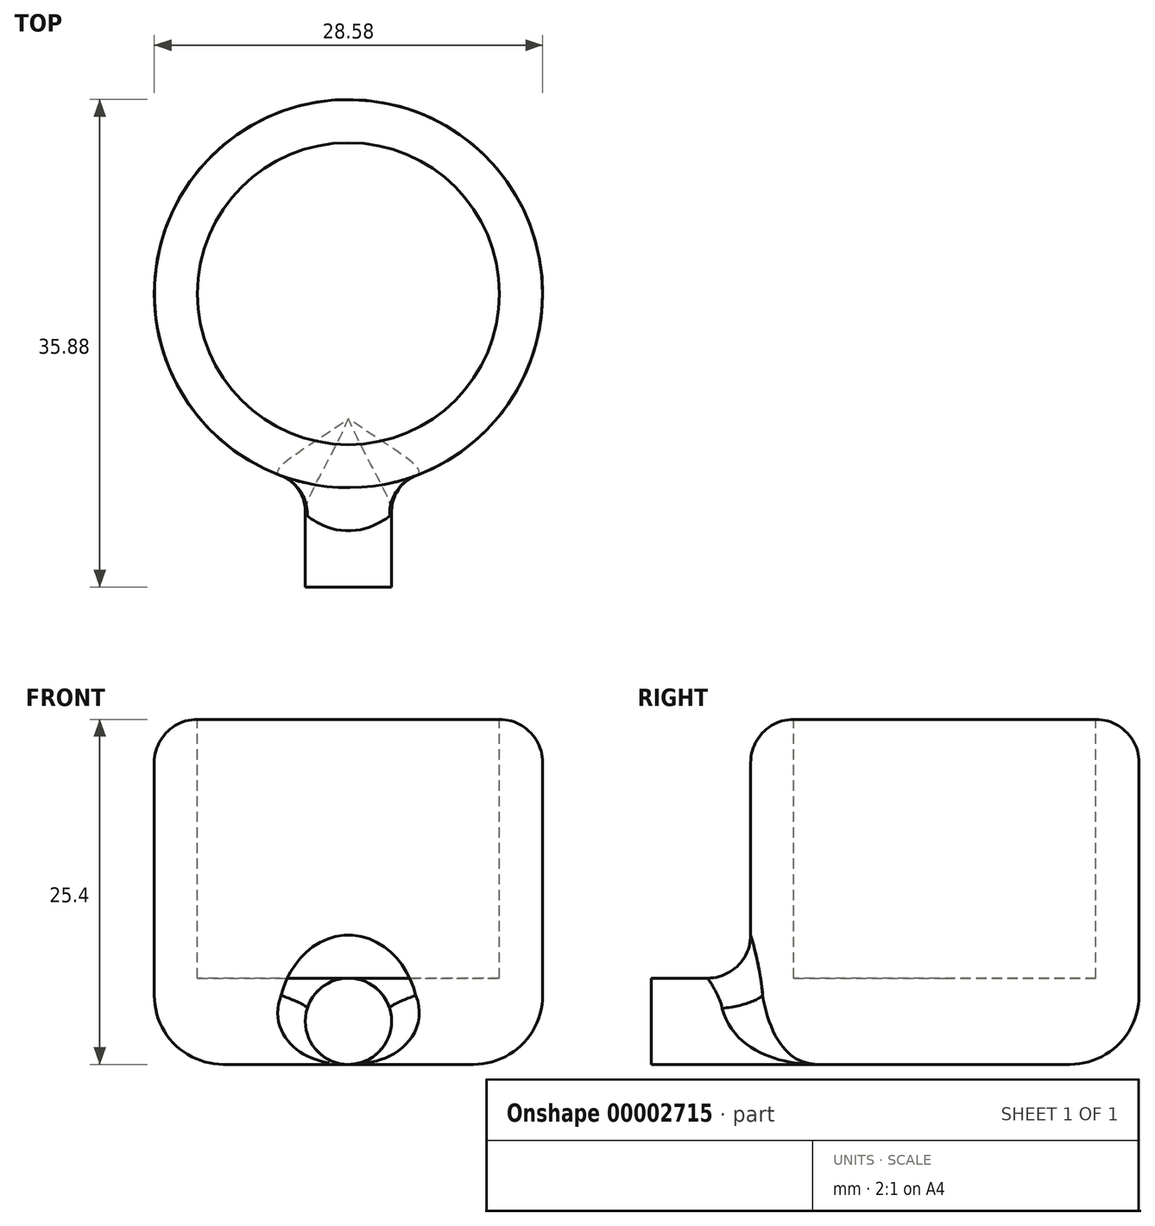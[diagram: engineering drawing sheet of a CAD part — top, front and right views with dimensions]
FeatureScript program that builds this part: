
annotation { "Feature Type Name" : "Feature", "Feature Type Description" : "" }
export const myFeature = defineFeature(function(context is Context, id is Id, definition is map)
    precondition{}
    {
        {
            var Q0;
            Q0=qCreatedBy(makeId("Top.planeOp"),FACE);
            var sketch = newSketch(context, id + "F0", { "sketchPlane" : qUnion([Q0])});
            skCircle(sketch, "E0", {"center": v(0, 0) * mm, "radius": 14.29 * mm});
            skSolve(sketch);
        }
        {
            var Q0;
            Q0=makeQuery(id+"F0.imprint","IMPRINT",FACE,{"disambiguationData":[TD([[makeQuery(id+"F0.imprint","IMPRINT",EDGE,{"derivedFrom":sQuery(id+"F0.wireOp",EDGE,"E0")}),1.0]])]});
            extrude(context, id + "F1", {"entities" : qUnion([Q0]), "depth" : 25.4 * mm});
        }
        {
            var Q0;
            Q0=qCreatedBy(makeId("Front.planeOp"),FACE);
            var sketch = newSketch(context, id + "F2", { "sketchPlane" : qUnion([Q0])});
            skCircle(sketch, "E1", {"center": v(0, 3.18) * mm, "radius": 3.18 * mm});
            skSolve(sketch);
        }
        {
            var Q0;
            Q0=makeQuery(id+"F2.imprint","IMPRINT",FACE,{"disambiguationData":[TD([[makeQuery(id+"F2.imprint","IMPRINT",EDGE,{"derivedFrom":sQuery(id+"F2.wireOp",EDGE,"E1")}),1.0]])]});
            extrude(context, id + "F3", {"entities" : qUnion([Q0]), "operationType" : NewBodyOperationType.ADD, "depth" : 21.59 * mm});
        }
        {
            var Q0;
            Q0=makeQuery(id+"F1.opExtrude","CAP_FACE",FACE,{"disambiguationData":[OSD([sQuery(id+"F0.wireOp",EDGE,"E0")])],"isStart":false});
            var sketch = newSketch(context, id + "F4", { "sketchPlane" : qUnion([Q0])});
            skCircle(sketch, "E2", {"center": v(0, 0) * mm, "radius": 11.11 * mm});
            skSolve(sketch);
        }
        {
            var Q0;
            Q0=makeQuery(id+"F4.imprint","IMPRINT",FACE,{"disambiguationData":[TD([[makeQuery(id+"F4.imprint","IMPRINT",EDGE,{"derivedFrom":sQuery(id+"F4.wireOp",EDGE,"E2")}),1.0]])]});
            extrude(context, id + "F5", {"entities" : qUnion([Q0]), "operationType" : NewBodyOperationType.REMOVE, "oppositeDirection" : true, "depth" : 19.05 * mm});
        }
        {
            var Q0;
            Q0=makeQuery(id+"F1.opExtrude","CAP_EDGE",EDGE,{"disambiguationData":[OSD([sQuery(id+"F0.wireOp",EDGE,"E0")])],"isStart":true});
            fillet(context, id + "F6", {"entities" : qUnion([Q0]), "radius" : 5.08 * mm, "tangentPropagation" : true, "allowEdgeOverflow" : false});
        }
        {
            var Q0;
            Q0=makeQuery(id+"F1.opExtrude","SWEPT_FACE",FACE,{"disambiguationData":[OSD([sQuery(id+"F0.wireOp",EDGE,"E0")])]});
            fillet(context, id + "F7", {"entities" : qUnion([Q0]), "radius" : 3.17 * mm, "tangentPropagation" : true, "allowEdgeOverflow" : false});
        }
    });
